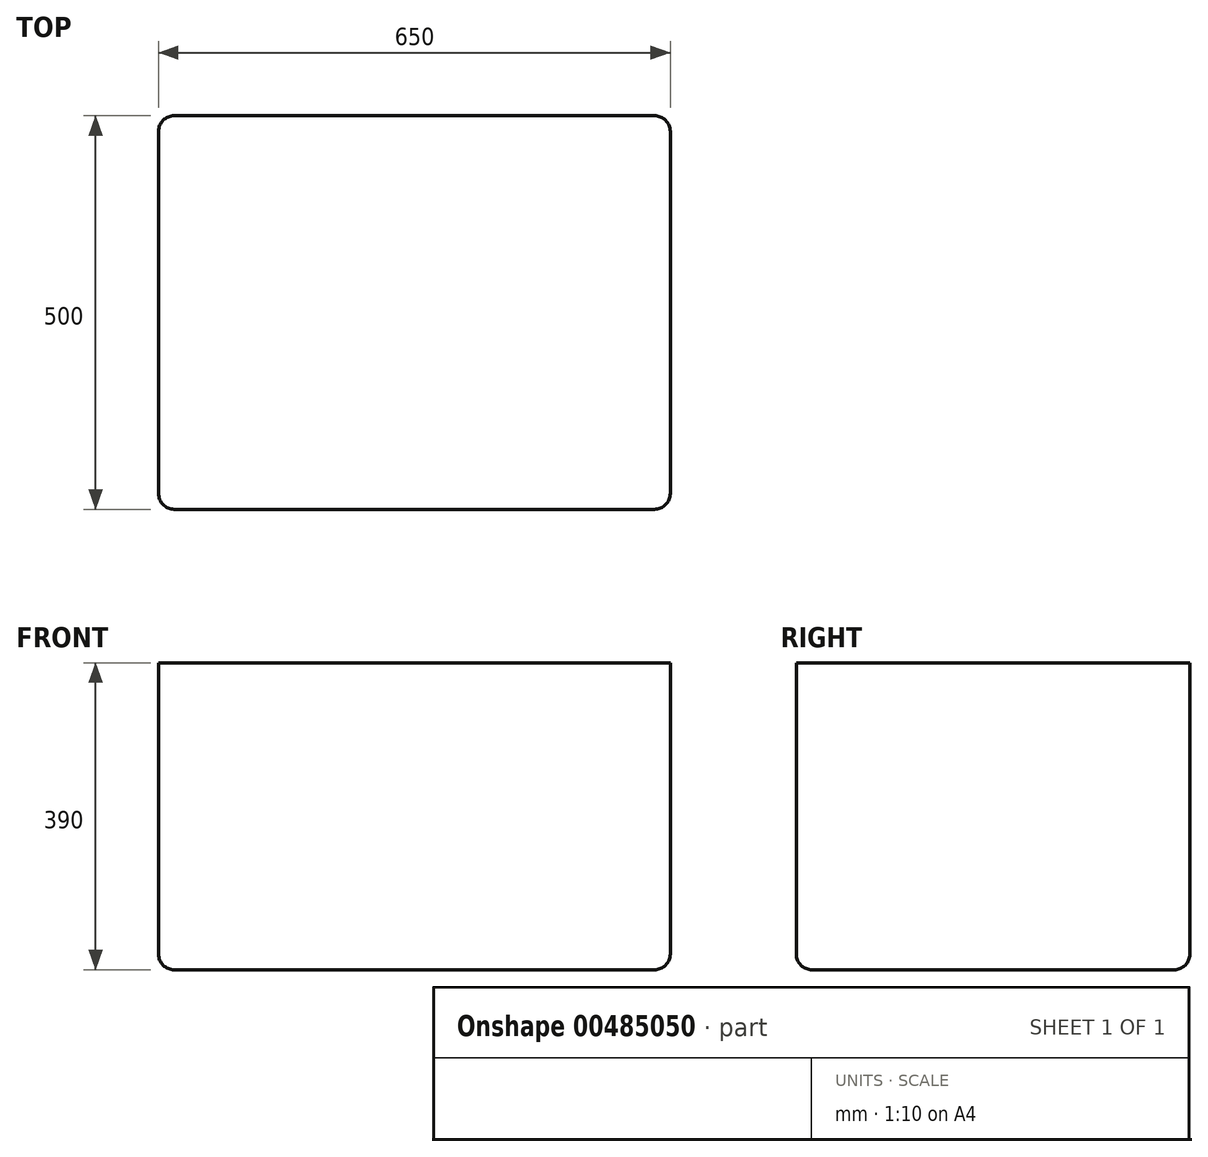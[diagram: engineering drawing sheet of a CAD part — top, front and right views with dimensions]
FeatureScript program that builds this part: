
annotation { "Feature Type Name" : "Feature", "Feature Type Description" : "" }
export const myFeature = defineFeature(function(context is Context, id is Id, definition is map)
    precondition{}
    {
        {
            var Q0;
            Q0=qCreatedBy(makeId("Top.planeOp"),FACE);
            var sketch = newSketch(context, id + "F0", { "sketchPlane" : qUnion([Q0])});
            skLineSegment(sketch, "E0.bottom", {"start": v(325, -250) * mm, "end": v(-325, -250) * mm});
            skLineSegment(sketch, "E0.top", {"start": v(325, 250) * mm, "end": v(-325, 250) * mm});
            skLineSegment(sketch, "E0.left", {"start": v(325, -250) * mm, "end": v(325, 250) * mm});
            skLineSegment(sketch, "E0.right", {"start": v(-325, -250) * mm, "end": v(-325, 250) * mm});
            skPoint(sketch, "E0.middle", {"position": v(0, 0) * mm});
            skSolve(sketch);
        }
        {
            var Q0;
            Q0=qSketchRegion(id+"F0",true);
            extrude(context, id + "F1", {"entities" : qUnion([Q0]), "depth" : 390 * mm});
        }
        {
            var Q0;
            Q0=makeQuery(id+"F1.opExtrude","SWEPT_EDGE",EDGE,{"disambiguationData":[OSD([sQuery(id+"F0.wireOp",EDGE,"E0.bottom"),sQuery(id+"F0.wireOp",EDGE,"E0.left")])]});
            var Q1;
            Q1=makeQuery(id+"F1.opExtrude","SWEPT_EDGE",EDGE,{"disambiguationData":[OSD([sQuery(id+"F0.wireOp",EDGE,"E0.top"),sQuery(id+"F0.wireOp",EDGE,"E0.left")])]});
            var Q2;
            Q2=makeQuery(id+"F1.opExtrude","SWEPT_EDGE",EDGE,{"disambiguationData":[OSD([sQuery(id+"F0.wireOp",EDGE,"E0.bottom"),sQuery(id+"F0.wireOp",EDGE,"E0.right")])]});
            var Q3;
            Q3=makeQuery(id+"F1.opExtrude","SWEPT_EDGE",EDGE,{"disambiguationData":[OSD([sQuery(id+"F0.wireOp",EDGE,"E0.top"),sQuery(id+"F0.wireOp",EDGE,"E0.right")])]});
            var Q4;
            Q4=makeQuery(id+"F1.opExtrude","CAP_FACE",FACE,{"disambiguationData":[OSD([sQuery(id+"F0.wireOp",EDGE,"E0.bottom"),sQuery(id+"F0.wireOp",EDGE,"E0.top"),sQuery(id+"F0.wireOp",EDGE,"E0.left"),sQuery(id+"F0.wireOp",EDGE,"E0.right")])],"isStart":true});
            fillet(context, id + "F3", {"entities" : qUnion([Q0, Q1, Q2, Q3, Q4]), "radius" : 20 * mm, "tangentPropagation" : true, "allowEdgeOverflow" : false});
        }
    });
